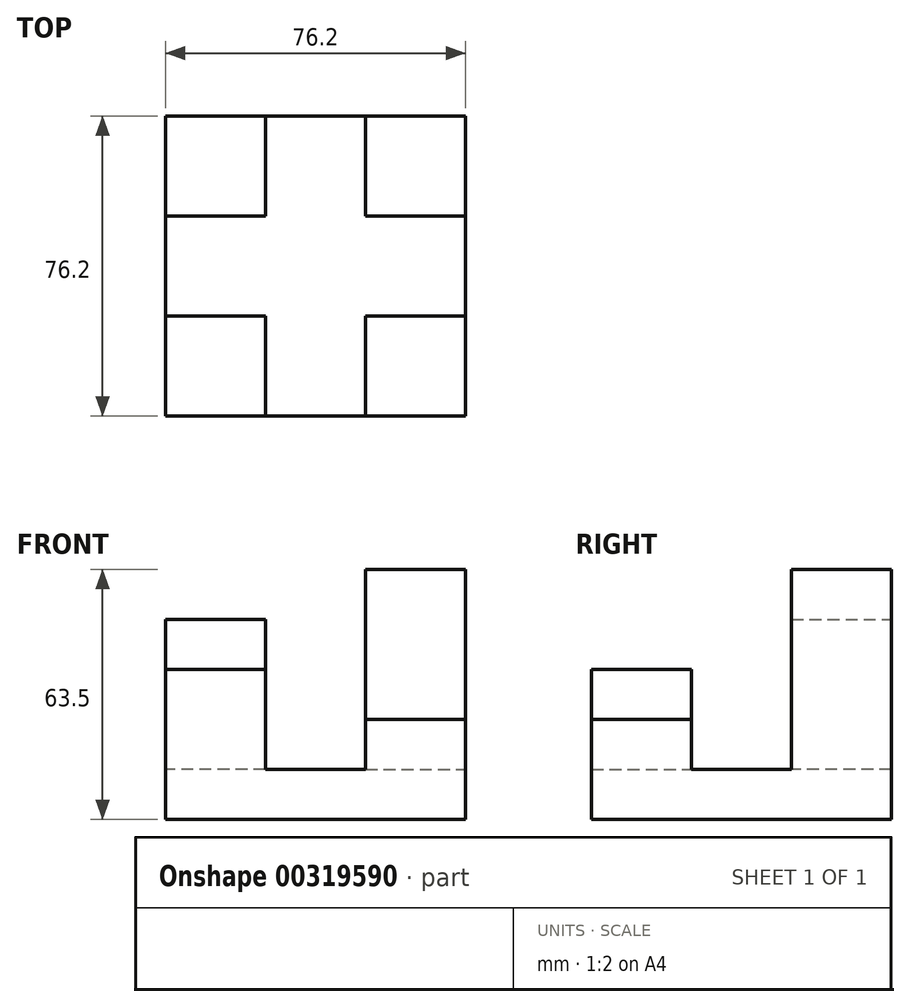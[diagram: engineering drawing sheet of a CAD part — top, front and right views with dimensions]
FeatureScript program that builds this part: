
annotation { "Feature Type Name" : "Feature", "Feature Type Description" : "" }
export const myFeature = defineFeature(function(context is Context, id is Id, definition is map)
    precondition{}
    {
        {
            var Q0;
            Q0=qCreatedBy(makeId("Front.planeOp"),FACE);
            var sketch = newSketch(context, id + "F0", { "sketchPlane" : qUnion([Q0])});
            skLineSegment(sketch, "E0", {"start": v(-29.93, -39.55) * mm, "end": v(46.27, -39.55) * mm});
            skLineSegment(sketch, "E1", {"start": v(-29.93, -39.55) * mm, "end": v(-29.93, -26.85) * mm});
            skLineSegment(sketch, "E2", {"start": v(-29.93, -26.85) * mm, "end": v(46.27, -26.85) * mm});
            skLineSegment(sketch, "E3", {"start": v(46.27, -26.85) * mm, "end": v(46.27, -39.55) * mm});
            skSolve(sketch);
        }
        {
            var Q0;
            Q0=makeQuery(id+"F0.imprint","IMPRINT",FACE,{"disambiguationData":[TD([[makeQuery(id+"F0.imprint","IMPRINT",EDGE,{"derivedFrom":sQuery(id+"F0.wireOp",EDGE,"E0")}),1.0]])]});
            extrude(context, id + "F1", {"entities" : qUnion([Q0]), "depth" : 76.2 * mm});
        }
        {
            var Q0;
            Q0=makeQuery(id+"F1.opExtrude","SWEPT_FACE",FACE,{"disambiguationData":[OSD([sQuery(id+"F0.wireOp",EDGE,"E2")])]});
            var sketch = newSketch(context, id + "F2", { "sketchPlane" : qUnion([Q0])});
            skLineSegment(sketch, "E4", {"start": v(46.27, -76.2) * mm, "end": v(20.87, -76.2) * mm});
            skLineSegment(sketch, "E5", {"start": v(20.87, -76.2) * mm, "end": v(20.87, -50.8) * mm});
            skLineSegment(sketch, "E6", {"start": v(20.87, -50.8) * mm, "end": v(46.27, -50.8) * mm});
            skLineSegment(sketch, "E7", {"start": v(46.27, -50.8) * mm, "end": v(46.27, -76.2) * mm});
            skLineSegment(sketch, "E8", {"start": v(-29.93, -76.2) * mm, "end": v(-4.53, -76.2) * mm});
            skLineSegment(sketch, "E9", {"start": v(-29.93, -76.2) * mm, "end": v(-29.93, -50.8) * mm});
            skLineSegment(sketch, "E10", {"start": v(-29.93, -50.8) * mm, "end": v(-4.53, -50.8) * mm});
            skLineSegment(sketch, "E11", {"start": v(-4.53, -50.8) * mm, "end": v(-4.53, -76.2) * mm});
            skLineSegment(sketch, "E12", {"start": v(-29.93, 0) * mm, "end": v(-4.53, 0) * mm});
            skLineSegment(sketch, "E13", {"start": v(-4.53, 0) * mm, "end": v(-4.53, -25.4) * mm});
            skLineSegment(sketch, "E14", {"start": v(-4.53, -25.4) * mm, "end": v(-29.93, -25.4) * mm});
            skLineSegment(sketch, "E15", {"start": v(-29.93, -25.4) * mm, "end": v(-29.93, 0) * mm});
            skLineSegment(sketch, "E16", {"start": v(46.27, 0) * mm, "end": v(20.87, 0) * mm});
            skLineSegment(sketch, "E17", {"start": v(20.87, 0) * mm, "end": v(20.87, -25.4) * mm});
            skLineSegment(sketch, "E18", {"start": v(20.87, -25.4) * mm, "end": v(46.27, -25.4) * mm});
            skLineSegment(sketch, "E19", {"start": v(46.27, -25.4) * mm, "end": v(46.27, 0) * mm});
            skSolve(sketch);
        }
        {
            var Q0;
            Q0=makeQuery(id+"F2.imprint","IMPRINT",FACE,{"disambiguationData":[TD([[makeQuery(id+"F2.imprint","IMPRINT",EDGE,{"derivedFrom":sQuery(id+"F2.wireOp",EDGE,"E16")}),-1.0]])]});
            extrude(context, id + "F3", {"entities" : qUnion([Q0]), "operationType" : NewBodyOperationType.ADD, "depth" : 50.8 * mm});
        }
        {
            var Q0;
            Q0=makeQuery(id+"F1.opExtrude","SWEPT_FACE",FACE,{"disambiguationData":[OSD([sQuery(id+"F0.wireOp",EDGE,"E2")])]});
            var sketch = newSketch(context, id + "F4", { "sketchPlane" : qUnion([Q0])});
            skLineSegment(sketch, "E20", {"start": v(-29.93, 0) * mm, "end": v(-4.53, 0) * mm});
            skLineSegment(sketch, "E21", {"start": v(-4.53, 0) * mm, "end": v(-4.53, -25.4) * mm});
            skLineSegment(sketch, "E22", {"start": v(-4.53, -25.4) * mm, "end": v(-29.93, -25.4) * mm});
            skLineSegment(sketch, "E23", {"start": v(-29.93, -25.4) * mm, "end": v(-29.93, 0) * mm});
            skSolve(sketch);
        }
        {
            var Q0;
            Q0=makeQuery(id+"F4.imprint","IMPRINT",FACE,{"disambiguationData":[TD([[makeQuery(id+"F4.imprint","IMPRINT",EDGE,{"derivedFrom":sQuery(id+"F4.wireOp",EDGE,"E20")}),-1.0]])]});
            extrude(context, id + "F5", {"entities" : qUnion([Q0]), "operationType" : NewBodyOperationType.ADD, "depth" : 38.1 * mm});
        }
        {
            var Q0;
            Q0=makeQuery(id+"F1.opExtrude","SWEPT_FACE",FACE,{"disambiguationData":[OSD([sQuery(id+"F0.wireOp",EDGE,"E2")])]});
            var sketch = newSketch(context, id + "F6", { "sketchPlane" : qUnion([Q0])});
            skLineSegment(sketch, "E24", {"start": v(-29.93, -76.2) * mm, "end": v(-4.53, -76.2) * mm});
            skLineSegment(sketch, "E25", {"start": v(-4.53, -76.2) * mm, "end": v(-4.53, -50.8) * mm});
            skLineSegment(sketch, "E26", {"start": v(-4.53, -50.8) * mm, "end": v(-29.93, -50.8) * mm});
            skLineSegment(sketch, "E27", {"start": v(-29.93, -50.8) * mm, "end": v(-29.93, -76.2) * mm});
            skSolve(sketch);
        }
        {
            var Q0;
            Q0=makeQuery(id+"F6.imprint","IMPRINT",FACE,{"disambiguationData":[TD([[makeQuery(id+"F6.imprint","IMPRINT",EDGE,{"derivedFrom":sQuery(id+"F6.wireOp",EDGE,"E24")}),1.0]])]});
            extrude(context, id + "F7", {"entities" : qUnion([Q0]), "operationType" : NewBodyOperationType.ADD, "depth" : 25.4 * mm});
        }
        {
            var Q0;
            Q0=makeQuery(id+"F1.opExtrude","SWEPT_FACE",FACE,{"disambiguationData":[OSD([sQuery(id+"F0.wireOp",EDGE,"E2")])]});
            var sketch = newSketch(context, id + "F8", { "sketchPlane" : qUnion([Q0])});
            skLineSegment(sketch, "E28", {"start": v(46.27, -76.2) * mm, "end": v(20.87, -76.2) * mm});
            skLineSegment(sketch, "E29", {"start": v(20.87, -76.2) * mm, "end": v(20.87, -50.8) * mm});
            skLineSegment(sketch, "E30", {"start": v(20.87, -50.8) * mm, "end": v(46.27, -50.8) * mm});
            skLineSegment(sketch, "E31", {"start": v(46.27, -50.8) * mm, "end": v(46.27, -76.2) * mm});
            skSolve(sketch);
        }
        {
            var Q0;
            Q0=makeQuery(id+"F8.imprint","IMPRINT",FACE,{"disambiguationData":[TD([[makeQuery(id+"F8.imprint","IMPRINT",EDGE,{"derivedFrom":sQuery(id+"F8.wireOp",EDGE,"E28")}),1.0]])]});
            extrude(context, id + "F9", {"entities" : qUnion([Q0]), "operationType" : NewBodyOperationType.ADD, "depth" : 12.7 * mm});
        }
    });
